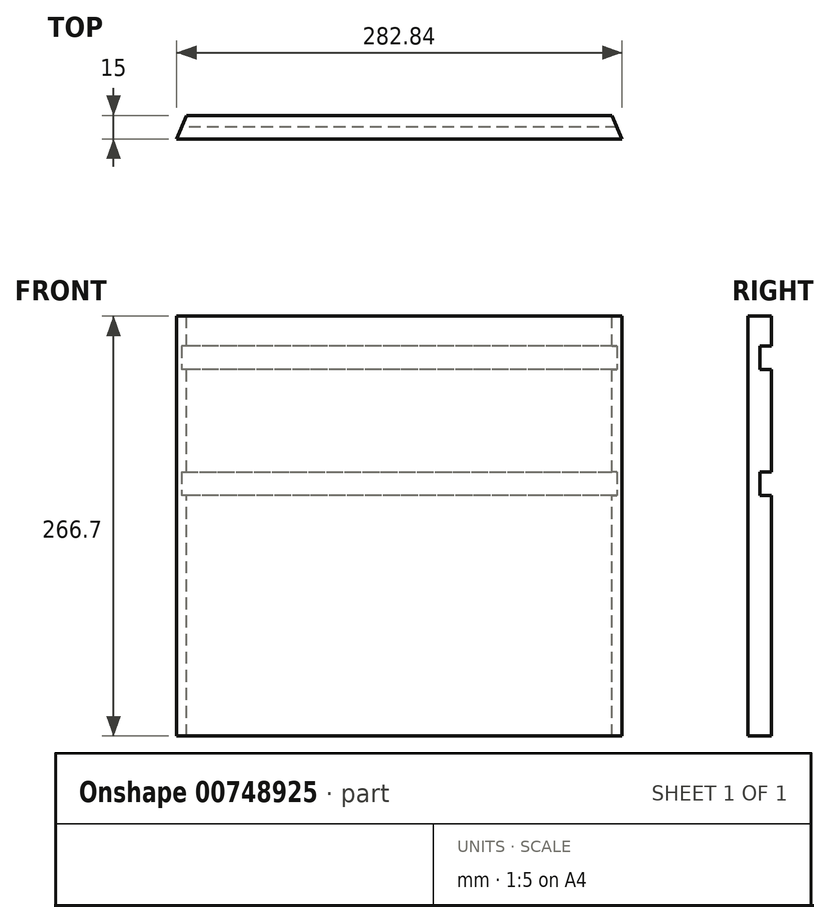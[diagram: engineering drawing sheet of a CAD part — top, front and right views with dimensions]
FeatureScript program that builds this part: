
annotation { "Feature Type Name" : "Feature", "Feature Type Description" : "" }
export const myFeature = defineFeature(function(context is Context, id is Id, definition is map)
    precondition{}
    {
        {
            var Q0;
            Q0=qCreatedBy(makeId("Top.planeOp"),FACE);
            var sketch = newSketch(context, id + "F0", { "sketchPlane" : qUnion([Q0])});
            skLineSegment(sketch, "E0.top", {"start": v(128.14, -11.81) * mm, "end": v(-142.28, -11.81) * mm});
            skLineSegment(sketch, "E1", {"start": v(-7.07, -11.81) * mm, "end": v(-7.07, -28.37) * mm, "construction": true});
            skLineSegment(sketch, "E2", {"start": v(109, 3.19) * mm, "end": v(-35.23, 3.19) * mm});
            skLineSegment(sketch, "E3.trimOffspring", {"start": v(-30.44, 3.19) * mm, "end": v(-123.14, 3.19) * mm});
            skLineSegment(sketch, "E4", {"start": v(-30.44, 3.19) * mm, "end": v(-35.23, 3.19) * mm});
            skLineSegment(sketch, "E5", {"start": v(109, 3.19) * mm, "end": v(128.14, 3.19) * mm});
            skLineSegment(sketch, "E6.MirrorCS", {"start": v(-123.14, 3.19) * mm, "end": v(-142.28, 3.19) * mm});
            skPoint(sketch, "E7.orphan", {"position": v(-171.78, 3.19) * mm});
            skPoint(sketch, "E8.end.orphan", {"position": v(157.63, 3.19) * mm});
            skLineSegment(sketch, "E9", {"start": v(-142.28, 3.19) * mm, "end": v(-148.5, -11.81) * mm});
            skLineSegment(sketch, "E10", {"start": v(-148.5, -11.81) * mm, "end": v(-142.28, -11.81) * mm});
            skLineSegment(sketch, "E11", {"start": v(128.14, 3.19) * mm, "end": v(134.35, -11.81) * mm});
            skLineSegment(sketch, "E12", {"start": v(134.35, -11.81) * mm, "end": v(128.14, -11.81) * mm});
            skSolve(sketch);
        }
        {
            var Q0;
            Q0=makeQuery(id+"F0.imprint","IMPRINT",FACE,{"disambiguationData":[TD([[makeQuery(id+"F0.imprint","IMPRINT",EDGE,{"derivedFrom":sQuery(id+"F0.wireOp",EDGE,"E0.top")}),-1.0]])]});
            extrude(context, id + "F1", {"entities" : qUnion([Q0]), "oppositeDirection" : true, "depth" : 266.7 * mm, "offsetDistance" : 25 * mm, "symmetric" : true});
        }
        {
            var Q0;
            Q0=makeQuery(id+"F1.opExtrude","SWEPT_FACE",FACE,{"disambiguationData":[OSD([sQuery(id+"F0.wireOp",EDGE,"E2")])]});
            var sketch = newSketch(context, id + "F2", { "sketchPlane" : qUnion([Q0])});
            skLineSegment(sketch, "E13.MirrorCS", {"start": v(283, 19.35) * mm, "end": v(283, 34.35) * mm});
            skLineSegment(sketch, "E14.MirrorCS", {"start": v(-273, 19.35) * mm, "end": v(283, 19.35) * mm});
            skLineSegment(sketch, "E15.MirrorCS", {"start": v(283, 34.35) * mm, "end": v(-273, 34.35) * mm});
            skLineSegment(sketch, "E16.MirrorCS", {"start": v(-273, 34.35) * mm, "end": v(-273, 19.35) * mm});
            skLineSegment(sketch, "E17", {"start": v(-273, 114.35) * mm, "end": v(-273, 99.35) * mm});
            skLineSegment(sketch, "E18", {"start": v(-273, 99.35) * mm, "end": v(283, 99.35) * mm});
            skLineSegment(sketch, "E19", {"start": v(-273, 114.35) * mm, "end": v(283, 114.35) * mm});
            skLineSegment(sketch, "E20", {"start": v(283, 114.35) * mm, "end": v(283, 99.35) * mm});
            skSolve(sketch);
        }
        {
            var Q0;
            Q0=qSketchRegion(id+"F2",true);
            extrude(context, id + "F3", {"entities" : qUnion([Q0]), "operationType" : NewBodyOperationType.REMOVE, "oppositeDirection" : true, "depth" : 7.5 * mm, "offsetDistance" : 25 * mm});
        }
    });
